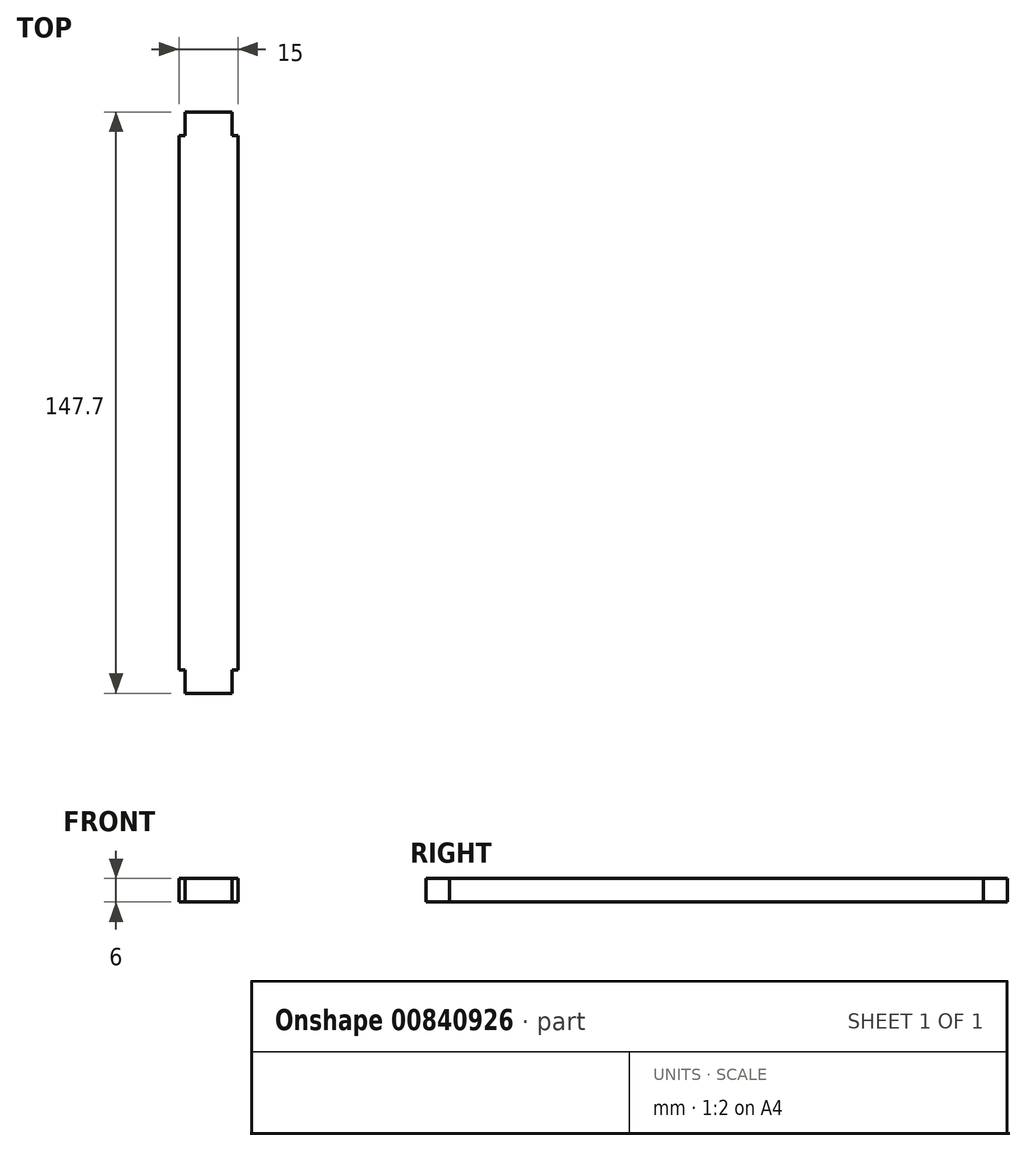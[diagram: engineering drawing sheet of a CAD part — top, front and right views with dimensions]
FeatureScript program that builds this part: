
annotation { "Feature Type Name" : "Feature", "Feature Type Description" : "" }
export const myFeature = defineFeature(function(context is Context, id is Id, definition is map)
    precondition{}
    {
        {
            var Q0;
            Q0=qCreatedBy(makeId("Top.planeOp"),FACE);
            var sketch = newSketch(context, id + "F0", { "sketchPlane" : qUnion([Q0])});
            skLineSegment(sketch, "E0", {"start": v(-17.4, 0) * mm, "end": v(22.4, 0) * mm, "construction": true});
            skLineSegment(sketch, "E1", {"start": v(-7.5, 0) * mm, "end": v(-7.5, 67.85) * mm});
            skLineSegment(sketch, "E2", {"start": v(-7.5, 67.85) * mm, "end": v(-6, 67.85) * mm});
            skLineSegment(sketch, "E3", {"start": v(-6, 67.85) * mm, "end": v(-6, 73.85) * mm});
            skLineSegment(sketch, "E4", {"start": v(-6, 73.85) * mm, "end": v(0, 73.85) * mm});
            skLineSegment(sketch, "E5", {"start": v(0, 73.85) * mm, "end": v(0, 0) * mm, "construction": true});
            skLineSegment(sketch, "E6.MirrorCS", {"start": v(7.5, 67.85) * mm, "end": v(6, 67.85) * mm});
            skLineSegment(sketch, "E7.MirrorCS", {"start": v(6, 67.85) * mm, "end": v(6, 73.85) * mm});
            skLineSegment(sketch, "E8.MirrorCS", {"start": v(6, 73.85) * mm, "end": v(0, 73.85) * mm});
            skLineSegment(sketch, "E9.MirrorCS", {"start": v(7.5, 0) * mm, "end": v(7.5, 67.85) * mm});
            skLineSegment(sketch, "E10.MirrorCS", {"start": v(-7.5, -67.85) * mm, "end": v(-6, -67.85) * mm});
            skLineSegment(sketch, "E11.MirrorCS", {"start": v(6, -67.85) * mm, "end": v(6, -73.85) * mm});
            skLineSegment(sketch, "E12.MirrorCS", {"start": v(-6, -67.85) * mm, "end": v(-6, -73.85) * mm});
            skLineSegment(sketch, "E13.MirrorCS", {"start": v(7.5, -67.85) * mm, "end": v(6, -67.85) * mm});
            skLineSegment(sketch, "E14.MirrorCS", {"start": v(-6, -73.85) * mm, "end": v(0, -73.85) * mm});
            skLineSegment(sketch, "E15.MirrorCS", {"start": v(6, -73.85) * mm, "end": v(0, -73.85) * mm});
            skLineSegment(sketch, "E16.MirrorCS", {"start": v(-7.5, 0) * mm, "end": v(-7.5, -67.85) * mm});
            skLineSegment(sketch, "E17.MirrorCS", {"start": v(0, -73.85) * mm, "end": v(0, 0) * mm, "construction": true});
            skLineSegment(sketch, "E18.MirrorCS", {"start": v(7.5, 0) * mm, "end": v(7.5, -67.85) * mm});
            skSolve(sketch);
        }
        {
            var Q0;
            Q0 = qSketchRegion(id + "F0", true);
            extrude(context, id + "F1", {"entities" : qUnion([Q0]), "depth" : 6 * mm, "offsetDistance" : 25 * mm});
        }
    });
